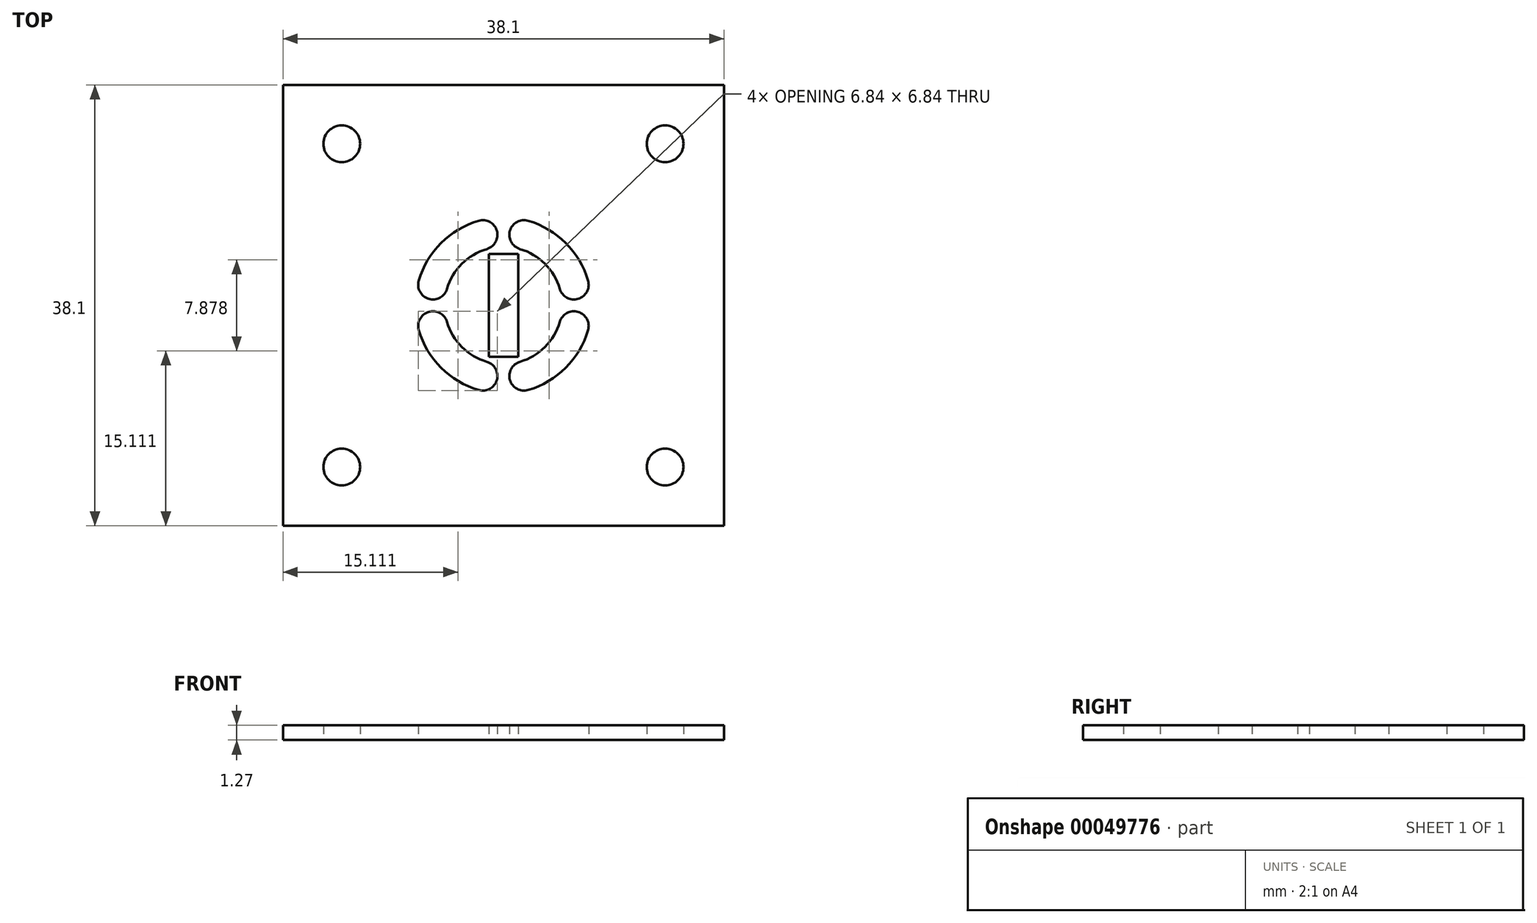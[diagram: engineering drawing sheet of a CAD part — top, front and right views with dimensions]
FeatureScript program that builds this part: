
annotation { "Feature Type Name" : "Feature", "Feature Type Description" : "" }
export const myFeature = defineFeature(function(context is Context, id is Id, definition is map)
    precondition{}
    {
        {
            var Q0;
            Q0=qCreatedBy(makeId("Top.planeOp"),FACE);
            var sketch = newSketch(context, id + "F0", { "sketchPlane" : qUnion([Q0])});
            skLineSegment(sketch, "E0.rect.bottom", {"start": v(19.05, -19.05) * mm, "end": v(-19.05, -19.05) * mm});
            skLineSegment(sketch, "E0.rect.top", {"start": v(19.05, 19.05) * mm, "end": v(-19.05, 19.05) * mm});
            skLineSegment(sketch, "E0.rect.left", {"start": v(19.05, -19.05) * mm, "end": v(19.05, 19.05) * mm});
            skLineSegment(sketch, "E0.rect.right", {"start": v(-19.05, -19.05) * mm, "end": v(-19.05, 19.05) * mm});
            skPoint(sketch, "E0.rect.middle", {"position": v(0, 0) * mm});
            skSolve(sketch);
        }
        {
            var Q0;
            Q0=qSketchRegion(id+"F0",true);
            extrude(context, id + "F1", {"entities" : qUnion([Q0]), "depth" : 1.27 * mm});
        }
        {
            var Q0;
            Q0=qCreatedBy(makeId("Top.planeOp"),FACE);
            var sketch = newSketch(context, id + "F2", { "sketchPlane" : qUnion([Q0])});
            skCircle(sketch, "E1", {"center": v(13.97, 13.97) * mm, "radius": 1.59 * mm});
            skSolve(sketch);
        }
        {
            var Q0;
            Q0=qSketchRegion(id+"F2",true);
            extrude(context, id + "F3", {"entities" : qUnion([Q0]), "operationType" : NewBodyOperationType.REMOVE, "depth" : 25.4 * mm});
        }
        {
            var Q0;
            Q0=makeQuery(id+"F1.opExtrude","SWEPT_BODY",BODY,{"disambiguationData":[OSD([sQuery(id+"F0.wireOp",EDGE,"E0.rect.bottom"),sQuery(id+"F0.wireOp",EDGE,"E0.rect.top"),sQuery(id+"F0.wireOp",EDGE,"E0.rect.left"),sQuery(id+"F0.wireOp",EDGE,"E0.rect.right")])]});
            var Q1;
            Q1=qCreatedBy(makeId("Right.planeOp"),FACE);
            mirror(context, id + "F4", {"operationType" : NewBodyOperationType.INTERSECT, "entities" : qUnion([Q0]), "mirrorPlane" : qUnion([Q1])});
        }
        {
            var Q0;
            Q0=makeQuery(id+"F1.opExtrude","SWEPT_BODY",BODY,{"disambiguationData":[OSD([sQuery(id+"F0.wireOp",EDGE,"E0.rect.bottom"),sQuery(id+"F0.wireOp",EDGE,"E0.rect.top"),sQuery(id+"F0.wireOp",EDGE,"E0.rect.left"),sQuery(id+"F0.wireOp",EDGE,"E0.rect.right")])]});
            var Q1;
            Q1=qCreatedBy(makeId("Front.planeOp"),FACE);
            mirror(context, id + "F5", {"operationType" : NewBodyOperationType.INTERSECT, "entities" : qUnion([Q0]), "mirrorPlane" : qUnion([Q1])});
        }
        {
            var Q0;
            Q0=qCreatedBy(makeId("Top.planeOp"),FACE);
            var sketch = newSketch(context, id + "F6", { "sketchPlane" : qUnion([Q0])});
            skArc(sketch, "E2", {"start": v(-7.31, -2.14) * mm, "mid": v(-5.39, -5.39) * mm, "end": v(-2.14, -7.31) * mm});
            skArc(sketch, "E3", {"start": v(0.63, -7.6) * mm, "mid": v(4.82, -5.9) * mm, "end": v(7.31, -2.14) * mm});
            skArc(sketch, "E4", {"start": v(7.31, 2.14) * mm, "mid": v(5.39, 5.39) * mm, "end": v(2.14, 7.31) * mm});
            skArc(sketch, "E5", {"start": v(-2.14, 7.31) * mm, "mid": v(-5.9, 4.82) * mm, "end": v(-7.6, 0.64) * mm});
            skArc(sketch, "E6", {"start": v(-1.43, 4.88) * mm, "mid": v(-3.6, 3.6) * mm, "end": v(-4.88, 1.43) * mm});
            skArc(sketch, "E7", {"start": v(4.88, 1.43) * mm, "mid": v(3.6, 3.6) * mm, "end": v(1.43, 4.88) * mm});
            skArc(sketch, "E8", {"start": v(1.43, -4.88) * mm, "mid": v(3.6, -3.6) * mm, "end": v(4.88, -1.43) * mm});
            skArc(sketch, "E9", {"start": v(-4.88, -1.43) * mm, "mid": v(-3.6, -3.6) * mm, "end": v(-1.43, -4.88) * mm});
            skLineSegment(sketch, "E10", {"start": v(-0.52, -6.2) * mm, "end": v(-0.52, -6.2) * mm});
            skLineSegment(sketch, "E11", {"start": v(0.52, -6.2) * mm, "end": v(0.52, -6.2) * mm});
            skLineSegment(sketch, "E12", {"start": v(-6.2, -0.52) * mm, "end": v(-6.2, -0.52) * mm});
            skLineSegment(sketch, "E13", {"start": v(-6.2, 0.52) * mm, "end": v(-6.2, 0.52) * mm});
            skLineSegment(sketch, "E14", {"start": v(-0.52, 6.2) * mm, "end": v(-0.52, 6.2) * mm});
            skLineSegment(sketch, "E15", {"start": v(0.52, 6.2) * mm, "end": v(0.52, 6.2) * mm});
            skLineSegment(sketch, "E16", {"start": v(6.2, -0.52) * mm, "end": v(6.2, -0.52) * mm});
            skLineSegment(sketch, "E17", {"start": v(6.2, 0.52) * mm, "end": v(6.2, 0.52) * mm});
            skArc(sketch, "E18", {"start": v(2.14, -7.31) * mm, "mid": v(5.9, -4.82) * mm, "end": v(7.6, -0.64) * mm});
            skArc(sketch, "E19", {"start": v(5.06, 0.42) * mm, "mid": v(3.6, 3.6) * mm, "end": v(0.42, 5.06) * mm});
            skArc(sketch, "E20", {"start": v(-0.42, 5.06) * mm, "mid": v(-3.6, 3.6) * mm, "end": v(-5.06, 0.42) * mm});
            skArc(sketch, "E21", {"start": v(-5.06, -0.42) * mm, "mid": v(-3.6, -3.6) * mm, "end": v(-0.42, -5.06) * mm});
            skLineSegment(sketch, "E22", {"start": v(-7.6, -0.64) * mm, "end": v(-7.6, -0.64) * mm});
            skLineSegment(sketch, "E23", {"start": v(-0.63, -7.6) * mm, "end": v(-0.63, -7.6) * mm});
            skArc(sketch, "E24", {"start": v(-7.6, -0.64) * mm, "mid": v(-5.39, -5.39) * mm, "end": v(-0.63, -7.6) * mm});
            skLineSegment(sketch, "E25", {"start": v(-0.42, -5.06) * mm, "end": v(-0.42, -5.06) * mm});
            skArc(sketch, "E26", {"start": v(-0.63, 7.6) * mm, "mid": v(-4.82, 5.9) * mm, "end": v(-7.31, 2.14) * mm});
            skArc(sketch, "E27", {"start": v(7.6, 0.64) * mm, "mid": v(5.39, 5.39) * mm, "end": v(0.64, 7.6) * mm});
            skLineSegment(sketch, "E28", {"start": v(0.42, -5.06) * mm, "end": v(0.42, -5.06) * mm});
            skLineSegment(sketch, "E29.rect.bottom", {"start": v(-1.27, -4.44) * mm, "end": v(1.27, -4.44) * mm});
            skLineSegment(sketch, "E29.rect.top", {"start": v(-1.27, 4.45) * mm, "end": v(1.27, 4.45) * mm});
            skLineSegment(sketch, "E29.rect.left", {"start": v(-1.27, -4.44) * mm, "end": v(-1.27, 4.45) * mm});
            skLineSegment(sketch, "E29.rect.right", {"start": v(1.27, -4.44) * mm, "end": v(1.27, 4.45) * mm});
            skPoint(sketch, "E30.visualSharp", {"position": v(-7.6, 0.64) * mm});
            skArc(sketch, "E30.filletArc", {"start": v(-7.31, 2.14) * mm, "mid": v(-7.14, 1.07) * mm, "end": v(-6.2, 0.52) * mm});
            skPoint(sketch, "E31.visualSharp", {"position": v(-5.06, 0.42) * mm});
            skArc(sketch, "E31.filletArc", {"start": v(-6.2, 0.52) * mm, "mid": v(-5.38, 0.74) * mm, "end": v(-4.88, 1.43) * mm});
            skPoint(sketch, "E32.visualSharp", {"position": v(-0.63, 7.6) * mm});
            skArc(sketch, "E32.filletArc", {"start": v(-0.52, 6.2) * mm, "mid": v(-1.07, 7.14) * mm, "end": v(-2.14, 7.31) * mm});
            skPoint(sketch, "E33.visualSharp", {"position": v(-0.42, 5.06) * mm});
            skArc(sketch, "E33.filletArc", {"start": v(-1.43, 4.88) * mm, "mid": v(-0.74, 5.38) * mm, "end": v(-0.52, 6.2) * mm});
            skPoint(sketch, "E34.visualSharp", {"position": v(0.64, 7.6) * mm});
            skArc(sketch, "E34.filletArc", {"start": v(2.14, 7.31) * mm, "mid": v(1.07, 7.14) * mm, "end": v(0.52, 6.2) * mm});
            skPoint(sketch, "E35.visualSharp", {"position": v(0.42, 5.06) * mm});
            skArc(sketch, "E35.filletArc", {"start": v(0.52, 6.2) * mm, "mid": v(0.74, 5.38) * mm, "end": v(1.43, 4.88) * mm});
            skPoint(sketch, "E36.visualSharp", {"position": v(5.06, 0.42) * mm});
            skArc(sketch, "E36.filletArc", {"start": v(4.88, 1.43) * mm, "mid": v(5.38, 0.74) * mm, "end": v(6.2, 0.52) * mm});
            skPoint(sketch, "E37.visualSharp", {"position": v(7.6, 0.64) * mm});
            skArc(sketch, "E37.filletArc", {"start": v(6.2, 0.52) * mm, "mid": v(7.14, 1.07) * mm, "end": v(7.31, 2.14) * mm});
            skPoint(sketch, "E38.visualSharp", {"position": v(5.06, -0.42) * mm});
            skArc(sketch, "E38.filletArc", {"start": v(6.2, -0.52) * mm, "mid": v(5.38, -0.74) * mm, "end": v(4.88, -1.43) * mm});
            skPoint(sketch, "E39.visualSharp", {"position": v(7.6, -0.64) * mm});
            skArc(sketch, "E39.filletArc", {"start": v(7.31, -2.14) * mm, "mid": v(7.14, -1.07) * mm, "end": v(6.2, -0.52) * mm});
            skPoint(sketch, "E40.visualSharp", {"position": v(0.63, -7.6) * mm});
            skArc(sketch, "E40.filletArc", {"start": v(0.52, -6.2) * mm, "mid": v(1.07, -7.14) * mm, "end": v(2.14, -7.31) * mm});
            skPoint(sketch, "E41.visualSharp", {"position": v(0.42, -5.06) * mm});
            skArc(sketch, "E41.filletArc", {"start": v(1.43, -4.88) * mm, "mid": v(0.74, -5.38) * mm, "end": v(0.52, -6.2) * mm});
            skPoint(sketch, "E42.visualSharp", {"position": v(-0.42, -5.06) * mm});
            skArc(sketch, "E42.filletArc", {"start": v(-0.52, -6.2) * mm, "mid": v(-0.74, -5.38) * mm, "end": v(-1.43, -4.88) * mm});
            skPoint(sketch, "E43.visualSharp", {"position": v(-0.64, -7.6) * mm});
            skArc(sketch, "E43.filletArc", {"start": v(-2.14, -7.31) * mm, "mid": v(-1.07, -7.14) * mm, "end": v(-0.52, -6.2) * mm});
            skPoint(sketch, "E44.visualSharp", {"position": v(-7.6, -0.64) * mm});
            skArc(sketch, "E44.filletArc", {"start": v(-6.2, -0.52) * mm, "mid": v(-7.14, -1.07) * mm, "end": v(-7.31, -2.14) * mm});
            skPoint(sketch, "E45.visualSharp", {"position": v(-5.06, -0.42) * mm});
            skArc(sketch, "E45.filletArc", {"start": v(-4.88, -1.43) * mm, "mid": v(-5.38, -0.74) * mm, "end": v(-6.2, -0.52) * mm});
            skSolve(sketch);
        }
        {
            var Q0;
            Q0 = qSketchRegion(id + "F6", true);
            extrude(context, id + "F7", {"entities" : qUnion([Q0]), "operationType" : NewBodyOperationType.REMOVE, "depth" : 25.4 * mm});
        }
    });
